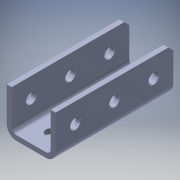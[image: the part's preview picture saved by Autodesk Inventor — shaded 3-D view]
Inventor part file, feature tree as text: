
AUTODESK INVENTOR PART (.ipt)
format: ipt  version: 2017 (Build 210142000, 142)  size: 243,200 bytes
history: native  units: in
note: dims shown in document units (in); Inventor stores cm internally (conversion verified against a paired STEP export)
features: extrude x1, sketch x1, other x1
ambient origin geometry x8: Origin, YZ Plane, XZ Plane, XY Plane, X Axis, Y Axis, Z Axis, Center Point
bodies: Solid1 (feature_tree)
feature tree (3):
  extrude  "Extrusion1"  [1 undecoded]
  sketch  "Sketch1"  dims[d0=69.0in d1=0.0in]
  other  "LPattern1"
note: 1 required parameter value undecoded (feature->parameter linkage not recoverable at this tier; creation-order binding heuristic only, values carry confidence <= 0.55)
